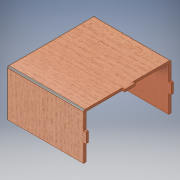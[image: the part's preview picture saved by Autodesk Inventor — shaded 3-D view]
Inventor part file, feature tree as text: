
AUTODESK INVENTOR PART (.ipt)
format: ipt  version: 2017 (Build 210142000, 142)  size: 226,304 bytes
history: native  units: in
note: dims shown in document units (in); Inventor stores cm internally (conversion verified against a paired STEP export)
features: extrude x6, sketch x4, fillet x4, hole x2
ambient origin geometry x8: Origin, YZ Plane, XZ Plane, XY Plane, X Axis, Y Axis, Z Axis, Center Point
bodies: Solid1 (feature_tree)
feature tree (16):
  extrude  "Extrusion1"  Depth=3.5433in
  extrude  "Extrusion2"  Depth=3.3558in TaperAngle=0.0deg
  sketch  "Sketch3"  dims[d11=0.1875in d12=3.3558in d13=0.0in]
  extrude  "Extrusion4"  Depth=3.3558in TaperAngle=0.0deg
  extrude  "Extrusion6"  Depth=5.9055in
  extrude  "Extrusion7"  Depth=6.6929in
  extrude  "Extrusion8"  Depth=0.1969in
  fillet  "Fillet3"  Radius=0.1969in
  fillet  "Fillet4"  Radius=2.9528in
  hole  "Hole3"  [1 undecoded]
  hole  "Hole4"  [1 undecoded]
  fillet  "Fillet5"  Radius=5.9055in
  fillet  "Fillet6"  Radius=0.1875in
  sketch  "Sketch1"  dims[d8=0.1875in d9=0.0in d10=3.5433in]
  sketch  "Sketch4"  dims[d17=0.1875in d18=3.3558in d19=0.0in]
  sketch  "Sketch7"  dims[d26=0.1875in d27=0.0in d28=5.9055in d29=6.6929in d30=0.1969in d31=0.1969in d32=2.9528in d33=2.9528in d34=0.7874in d35=5.9055in d36=0.1875in d37=3.3558in d38=0.0in d41=0.1875in d42=0.0in d63=0.1181in d64=0.1181in d65=1.0in d66=1.0in d67=0.0984in d68=0.75in d69=0.375in d70=0.25in d71=0.5635in d72=0.1969in d73=0.8108in d74=0.7874in d75=0.1969in d76=1.378in d77=1.378in d80=1.0in d81=1.0in d82=0.0984in d83=0.75in d84=0.375in d85=0.25in d86=0.5635in d87=0.1969in d88=0.8108in d89=0.0394in d90=0.7874in d91=0.1969in d92=1.378in d93=1.378in d94=0.0394in d43=1.0in d44=1.0in]
note: 2 required parameter values undecoded (feature->parameter linkage not recoverable at this tier; creation-order binding heuristic only, values carry confidence <= 0.55)
